# Revit family: CB32
name_source: partatom
category: Lighting Fixtures
revit_build: Autodesk Revit 2014 (Build: 20130308_1515(x64)
units: mm (PartAtom-declared; Revit-internal decimal feet)

## types (1)
- CB
    Apparent Load = 0 VA
    Assembly Code = D5020200
    Color Filter = 16777215
    Description = Compact Bollards feature full overlapping louvers which provides total source cutoff above horizontal. A soft glow from the louvers provides sufficient vertical illumination for gardens, pathways and of course, pedestrians.

Gasketed prismatic glass globe optimizes light output
Full cutoff above horizontal
Battery back-up, emergency battery pack and houseside shield options
    Diameter = 5 "
    Dimming Lamp Color Temperature Shift = <None>
    Finish = Powder Coat-Kim-White
    Glass = Glass-KIM-Temper Molded
    Height = 32 "
    Lamp = LED
    Load Classification = Lighting
    Manufacturer = Kim Lighting
    MasterFormat Title = Landscape Lighting, Site Lighting, Walkway Lighting
    Model = Compact Bollards
    Number of Poles = 1
    Photometric Notes = More IES files download on Photometric Web Link
    Photometric Web File = cb-20l4k.ies
    Photometric Web Link = https://www.hubbell.com
    Power Factor = 1
    Product Documentation Link = https://hubbellcdn.com
    Product Page URL = https://www.hubbell.com
    Radius = 2.5 "
    Series = Traditional Bollards
    Tilt Angle = 90.00°
    Type Comments = Lighted Bollard
    URL = https://www.hubbell.com
    Voltage = 120 V
    Wattage Comments = default

## geometry (parser evidence)
native form markers: Sweep x2
no freeform markers — native parametric forms only
